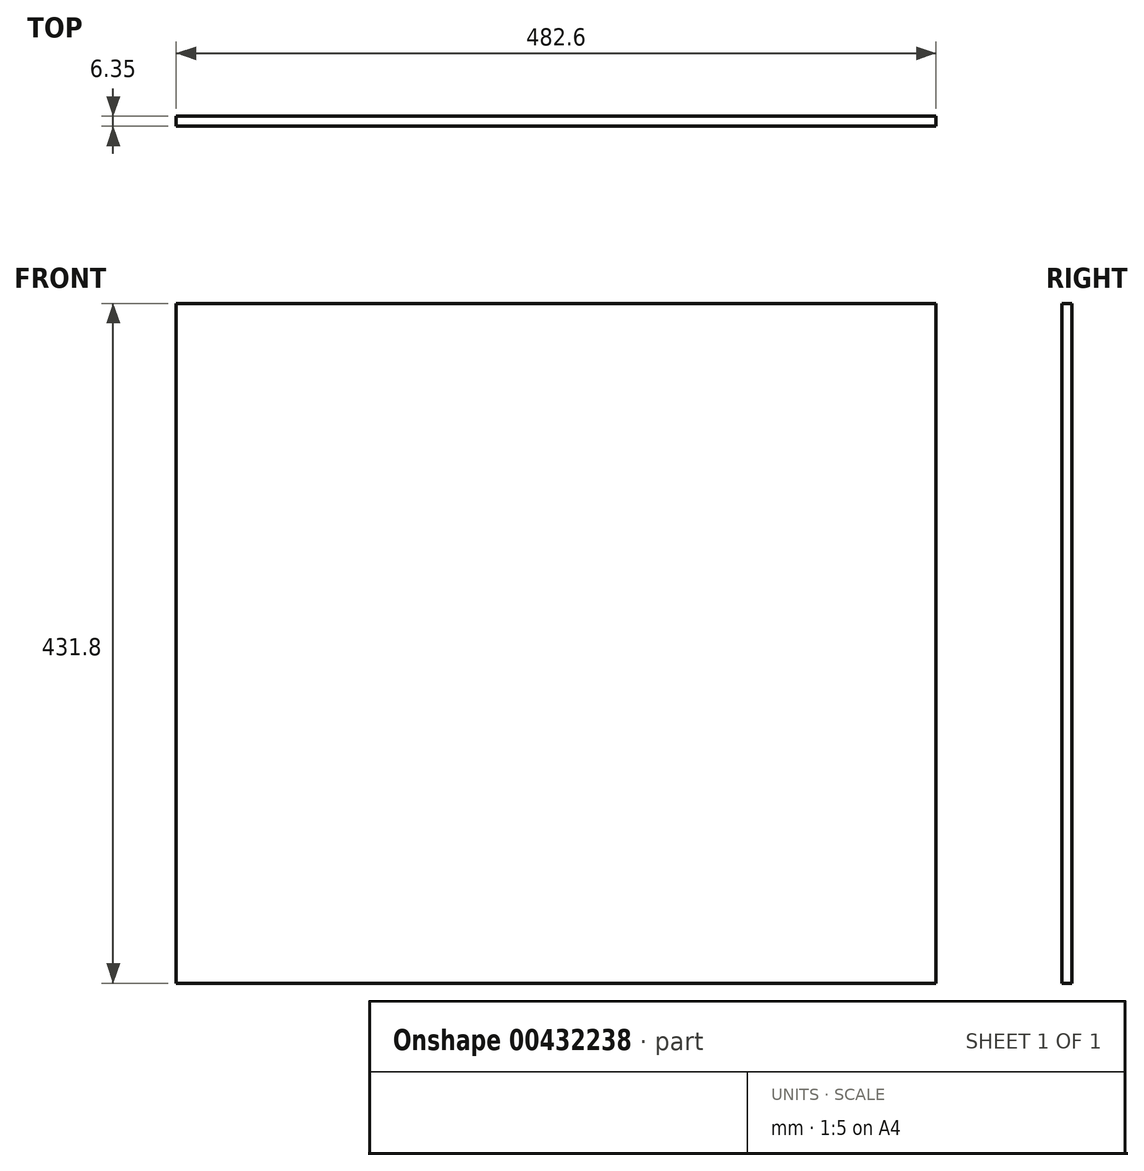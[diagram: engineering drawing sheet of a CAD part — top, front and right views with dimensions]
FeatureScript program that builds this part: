
annotation { "Feature Type Name" : "Feature", "Feature Type Description" : "" }
export const myFeature = defineFeature(function(context is Context, id is Id, definition is map)
    precondition{}
    {
        {
            var Q0;
            Q0=qCreatedBy(makeId("Right.planeOp"),FACE);
            var sketch = newSketch(context, id + "F0", { "sketchPlane" : qUnion([Q0])});
            skLineSegment(sketch, "E0", {"start": v(-5.29, 28.47) * mm, "end": v(1.06, 28.47) * mm});
            skLineSegment(sketch, "E1", {"start": v(1.06, 28.47) * mm, "end": v(1.06, -403.33) * mm});
            skLineSegment(sketch, "E2", {"start": v(-5.29, 28.47) * mm, "end": v(-5.29, -403.33) * mm});
            skLineSegment(sketch, "E3", {"start": v(-5.29, -403.33) * mm, "end": v(1.06, -403.33) * mm});
            skSolve(sketch);
        }
        {
            var Q0;
            Q0 = qSketchRegion(id + "F0", true);
            extrude(context, id + "F1", {"entities" : qUnion([Q0]), "depth" : 482.6 * mm});
        }
    });
